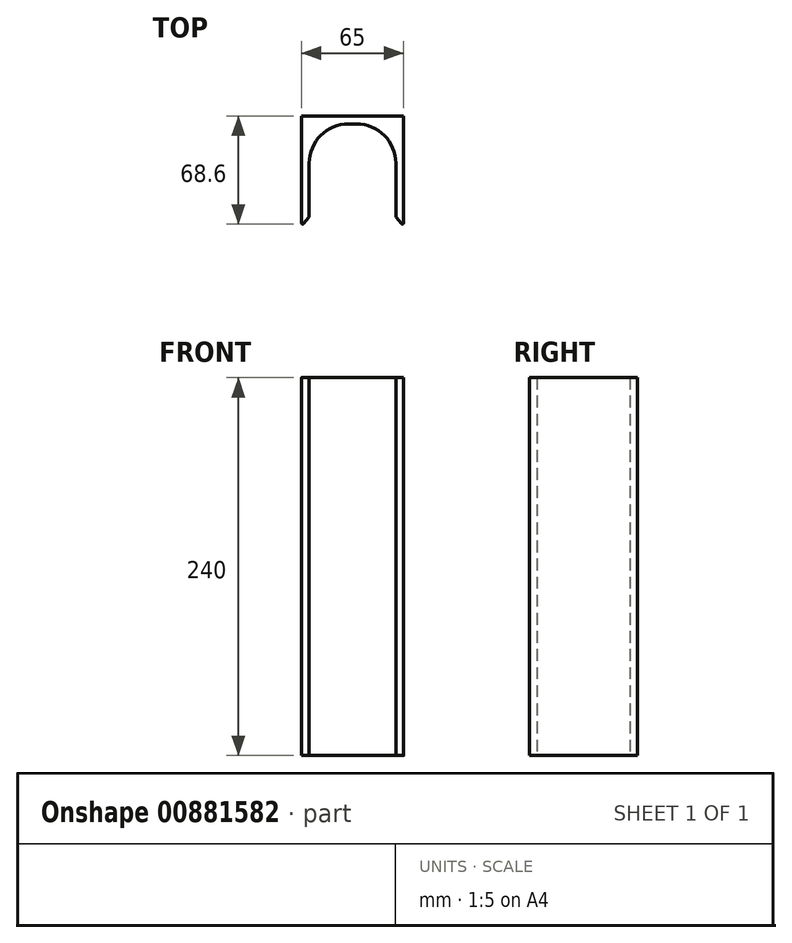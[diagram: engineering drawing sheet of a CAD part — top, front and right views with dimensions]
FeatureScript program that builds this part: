
annotation { "Feature Type Name" : "Feature", "Feature Type Description" : "" }
export const myFeature = defineFeature(function(context is Context, id is Id, definition is map)
    precondition{}
    {
        {
            var Q0;
            Q0=qCreatedBy(makeId("Top.planeOp"),FACE);
            var sketch = newSketch(context, id + "F0", { "sketchPlane" : qUnion([Q0])});
            skLineSegment(sketch, "E0.top", {"start": v(2.5, 27.5) * mm, "end": v(-2.5, 27.5) * mm});
            skLineSegment(sketch, "E0.left", {"start": v(27.5, -31.52) * mm, "end": v(27.5, 2.5) * mm});
            skLineSegment(sketch, "E0.right", {"start": v(-27.5, -31.52) * mm, "end": v(-27.5, 2.5) * mm});
            skPoint(sketch, "E0.middle", {"position": v(0, 0) * mm});
            skLineSegment(sketch, "E1.0", {"start": v(32.5, 32.5) * mm, "end": v(-32.5, 32.5) * mm});
            skLineSegment(sketch, "E2.0", {"start": v(27.5, -31.52) * mm, "end": v(-27.5, -31.52) * mm});
            skPoint(sketch, "E3.orphan", {"position": v(27.5, -27.5) * mm});
            skPoint(sketch, "E0.bottom.end.orphan", {"position": v(-27.5, -27.5) * mm});
            skPoint(sketch, "E4.visualSharp", {"position": v(-27.5, 27.5) * mm});
            skArc(sketch, "E4.filletArc", {"start": v(-2.5, 27.5) * mm, "mid": v(-20.18, 20.18) * mm, "end": v(-27.5, 2.5) * mm});
            skCircle(sketch, "E5", {"center": v(0, 0) * mm, "radius": 27.5 * mm});
            skPoint(sketch, "E6.visualSharp", {"position": v(27.5, 27.5) * mm});
            skArc(sketch, "E6.filletArc", {"start": v(27.5, 2.5) * mm, "mid": v(20.18, 20.18) * mm, "end": v(2.5, 27.5) * mm});
            skLineSegment(sketch, "E7", {"start": v(-32.5, 32.5) * mm, "end": v(-32.5, -32.5) * mm});
            skLineSegment(sketch, "E8", {"start": v(-32.5, -32.5) * mm, "end": v(-32.5, -35.3) * mm});
            skLineSegment(sketch, "E9", {"start": v(-27.5, -31.52) * mm, "end": v(-31.09, -35.81) * mm});
            skLineSegment(sketch, "E10", {"start": v(32.5, 32.5) * mm, "end": v(32.5, -32.5) * mm});
            skLineSegment(sketch, "E11", {"start": v(32.5, -32.5) * mm, "end": v(32.5, -35.3) * mm});
            skLineSegment(sketch, "E12", {"start": v(31.09, -35.81) * mm, "end": v(27.5, -31.52) * mm});
            skPoint(sketch, "E13.visualSharp", {"position": v(-32.5, -37.5) * mm});
            skArc(sketch, "E13.filletArc", {"start": v(-32.5, -35.3) * mm, "mid": v(-31.97, -36.05) * mm, "end": v(-31.09, -35.81) * mm});
            skPoint(sketch, "E14.visualSharp", {"position": v(32.5, -37.5) * mm});
            skArc(sketch, "E14.filletArc", {"start": v(31.09, -35.81) * mm, "mid": v(31.97, -36.05) * mm, "end": v(32.5, -35.3) * mm});
            skSolve(sketch);
        }
        {
            var Q0;
            Q0=makeQuery(id+"F0.imprint","IMPRINT",FACE,{"disambiguationData":[TD([[makeQuery(id+"F0.imprint","IMPRINT",EDGE,{"derivedFrom":sQuery(id+"F0.wireOp",EDGE,"E0.top")}),-1.0]])]});
            extrude(context, id + "F1", {"entities" : qUnion([Q0]), "depth" : 120 * mm, "offsetDistance" : 25 * mm, "hasSecondDirection" : true, "secondDirectionOppositeDirection" : true, "secondDirectionDepth" : 120 * mm});
        }
    });
